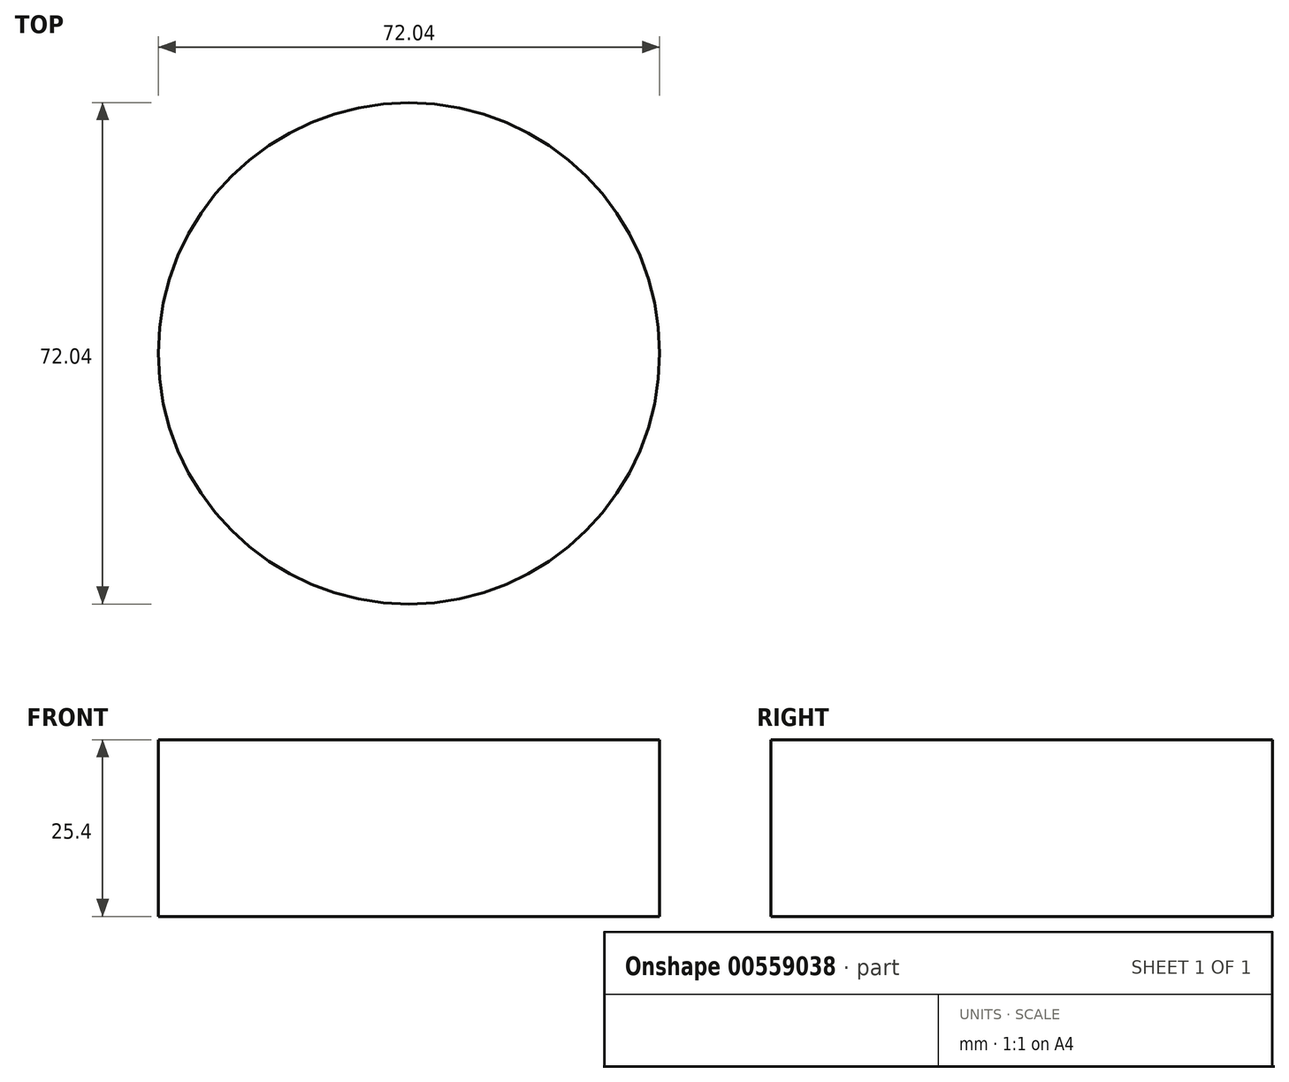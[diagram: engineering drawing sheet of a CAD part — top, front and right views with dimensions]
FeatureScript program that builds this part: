
annotation { "Feature Type Name" : "Feature", "Feature Type Description" : "" }
export const myFeature = defineFeature(function(context is Context, id is Id, definition is map)
    precondition{}
    {
        {
            var Q0;
            Q0=qCreatedBy(makeId("Top.planeOp"),FACE);
            var sketch = newSketch(context, id + "F0", { "sketchPlane" : qUnion([Q0])});
            skCircle(sketch, "E0", {"center": v(0, 0) * mm, "radius": 36.02 * mm});
            skSolve(sketch);
        }
        {
            var Q0;
            Q0=sQuery(id+"F0.wireOp",EDGE,"E0");
            extrude(context, id + "F1", {"bodyType" : ToolBodyType.SURFACE, "surfaceEntities" : qUnion([Q0]), "depth" : 25.4 * mm, "offsetDistance" : 25.4 * mm});
        }
    });
